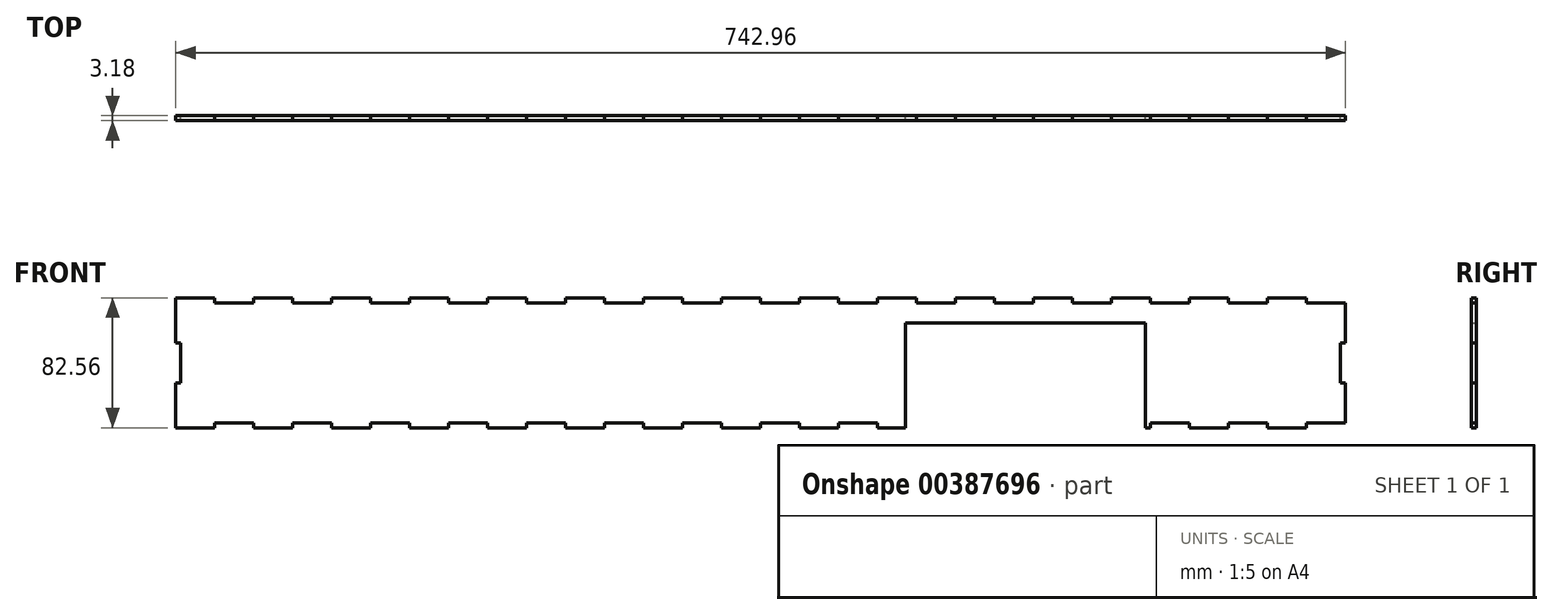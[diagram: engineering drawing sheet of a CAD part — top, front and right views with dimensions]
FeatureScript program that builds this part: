
annotation { "Feature Type Name" : "Feature", "Feature Type Description" : "" }
export const myFeature = defineFeature(function(context is Context, id is Id, definition is map)
    precondition{}
    {
        {
            var Q0;
            Q0=qCreatedBy(makeId("Front.planeOp"),FACE);
            var sketch = newSketch(context, id + "F0", { "sketchPlane" : qUnion([Q0])});
            skLineSegment(sketch, "E0.right", {"start": v(-371.48, -38.1) * mm, "end": v(-371.48, 38.1) * mm, "construction": true});
            skPoint(sketch, "E0.middle", {"position": v(0, 0) * mm});
            skLineSegment(sketch, "E1.top", {"start": v(244.47, 25.4) * mm, "end": v(92.07, 25.4) * mm});
            skLineSegment(sketch, "E1.left", {"start": v(244.47, -38.1) * mm, "end": v(244.47, 25.4) * mm});
            skLineSegment(sketch, "E1.right", {"start": v(92.07, -38.1) * mm, "end": v(92.07, 25.4) * mm});
            skPoint(sketch, "E1.middle", {"position": v(168.28, -6.35) * mm});
            skLineSegment(sketch, "E2.MirrorCS", {"start": v(123.83, 41.28) * mm, "end": v(123.83, 38.1) * mm});
            skLineSegment(sketch, "E3.MirrorCS", {"start": v(-247.65, 41.28) * mm, "end": v(-247.65, 38.1) * mm});
            skLineSegment(sketch, "E4.MirrorCS", {"start": v(272.42, 41.28) * mm, "end": v(272.42, 38.1) * mm});
            skLineSegment(sketch, "E5.MirrorCS", {"start": v(247.65, 41.28) * mm, "end": v(247.65, 38.1) * mm});
            skLineSegment(sketch, "E6.MirrorCS", {"start": v(-297.18, 41.28) * mm, "end": v(-297.18, 38.1) * mm});
            skLineSegment(sketch, "E7.MirrorCS", {"start": v(24.77, 41.28) * mm, "end": v(24.77, 38.1) * mm});
            skLineSegment(sketch, "E8.MirrorCS", {"start": v(-198.12, 41.28) * mm, "end": v(-198.12, 38.1) * mm});
            skLineSegment(sketch, "E9.MirrorCS", {"start": v(-49.53, 41.28) * mm, "end": v(-49.53, 38.1) * mm});
            skLineSegment(sketch, "E10.MirrorCS", {"start": v(222.89, 41.28) * mm, "end": v(222.89, 38.1) * mm});
            skLineSegment(sketch, "E11.MirrorCS", {"start": v(-74.3, 41.28) * mm, "end": v(-74.3, 38.1) * mm});
            skLineSegment(sketch, "E12.MirrorCS", {"start": v(-99.06, 41.28) * mm, "end": v(-99.06, 38.1) * mm});
            skLineSegment(sketch, "E13.MirrorCS", {"start": v(-148.59, 41.28) * mm, "end": v(-148.59, 38.1) * mm});
            skLineSegment(sketch, "E14.MirrorCS", {"start": v(-346.7, 41.28) * mm, "end": v(-346.7, 38.1) * mm});
            skLineSegment(sketch, "E15.MirrorCS", {"start": v(173.36, 41.28) * mm, "end": v(173.36, 38.1) * mm});
            skLineSegment(sketch, "E16.MirrorCS", {"start": v(-321.94, 41.28) * mm, "end": v(-321.94, 38.1) * mm});
            skLineSegment(sketch, "E17.MirrorCS", {"start": v(-123.82, 41.28) * mm, "end": v(-123.82, 38.1) * mm});
            skLineSegment(sketch, "E18.MirrorCS", {"start": v(-272.41, 41.28) * mm, "end": v(-272.41, 38.1) * mm});
            skLineSegment(sketch, "E19.MirrorCS", {"start": v(-173.35, 41.28) * mm, "end": v(-173.35, 38.1) * mm});
            skLineSegment(sketch, "E20.MirrorCS", {"start": v(198.12, 41.28) * mm, "end": v(198.12, 38.1) * mm});
            skLineSegment(sketch, "E21.MirrorCS", {"start": v(-24.76, 41.28) * mm, "end": v(-24.76, 38.1) * mm});
            skLineSegment(sketch, "E22.MirrorCS", {"start": v(74.3, 41.28) * mm, "end": v(74.3, 38.1) * mm});
            skLineSegment(sketch, "E23.MirrorCS", {"start": v(-222.88, 41.28) * mm, "end": v(-222.88, 38.1) * mm});
            skLineSegment(sketch, "E24.MirrorCS", {"start": v(346.71, 41.28) * mm, "end": v(346.71, 38.1) * mm});
            skLineSegment(sketch, "E25.MirrorCS", {"start": v(321.95, 41.28) * mm, "end": v(321.95, 38.1) * mm});
            skLineSegment(sketch, "E26.MirrorCS", {"start": v(297.18, 41.28) * mm, "end": v(297.18, 38.1) * mm});
            skLineSegment(sketch, "E27.MirrorCS", {"start": v(99.06, 41.28) * mm, "end": v(99.06, 38.1) * mm});
            skLineSegment(sketch, "E28.MirrorCS", {"start": v(148.6, 41.28) * mm, "end": v(148.6, 38.1) * mm});
            skLineSegment(sketch, "E29.MirrorCS", {"start": v(49.53, 41.28) * mm, "end": v(49.53, 38.1) * mm});
            skLineSegment(sketch, "E30.MirrorCS", {"start": v(0, 41.28) * mm, "end": v(0, 38.1) * mm});
            skLineSegment(sketch, "E31.MirrorCS", {"start": v(-272.41, 38.1) * mm, "end": v(-297.18, 38.1) * mm});
            skLineSegment(sketch, "E32.MirrorCS", {"start": v(-74.3, 38.1) * mm, "end": v(-99.06, 38.1) * mm});
            skLineSegment(sketch, "E33.MirrorCS", {"start": v(173.36, 38.1) * mm, "end": v(148.6, 38.1) * mm});
            skLineSegment(sketch, "E34.MirrorCS", {"start": v(-148.59, 41.28) * mm, "end": v(-173.35, 41.28) * mm});
            skLineSegment(sketch, "E35.MirrorCS", {"start": v(272.42, 38.1) * mm, "end": v(247.65, 38.1) * mm});
            skLineSegment(sketch, "E36.MirrorCS", {"start": v(24.77, 38.1) * mm, "end": v(0, 38.1) * mm});
            skLineSegment(sketch, "E37.MirrorCS", {"start": v(-198.12, 41.28) * mm, "end": v(-222.88, 41.28) * mm});
            skLineSegment(sketch, "E38.MirrorCS", {"start": v(-173.35, 38.1) * mm, "end": v(-198.12, 38.1) * mm});
            skLineSegment(sketch, "E39.MirrorCS", {"start": v(-24.76, 38.1) * mm, "end": v(-49.53, 38.1) * mm});
            skLineSegment(sketch, "E40.MirrorCS", {"start": v(222.89, 38.1) * mm, "end": v(198.12, 38.1) * mm});
            skLineSegment(sketch, "E41.MirrorCS", {"start": v(74.3, 38.1) * mm, "end": v(49.53, 38.1) * mm});
            skLineSegment(sketch, "E42.MirrorCS", {"start": v(-222.88, 38.1) * mm, "end": v(-247.65, 38.1) * mm});
            skLineSegment(sketch, "E43.MirrorCS", {"start": v(148.6, 41.28) * mm, "end": v(123.83, 41.28) * mm});
            skLineSegment(sketch, "E44.MirrorCS", {"start": v(99.06, 41.28) * mm, "end": v(74.3, 41.28) * mm});
            skLineSegment(sketch, "E45.MirrorCS", {"start": v(0, 41.28) * mm, "end": v(-24.76, 41.28) * mm});
            skLineSegment(sketch, "E46.MirrorCS", {"start": v(-99.06, 41.28) * mm, "end": v(-123.82, 41.28) * mm});
            skLineSegment(sketch, "E47.MirrorCS", {"start": v(123.83, 38.1) * mm, "end": v(99.06, 38.1) * mm});
            skLineSegment(sketch, "E48.MirrorCS", {"start": v(-297.18, 41.28) * mm, "end": v(-321.94, 41.28) * mm});
            skLineSegment(sketch, "E49.MirrorCS", {"start": v(198.12, 41.28) * mm, "end": v(173.36, 41.28) * mm});
            skLineSegment(sketch, "E50.MirrorCS", {"start": v(49.53, 41.28) * mm, "end": v(24.77, 41.28) * mm});
            skLineSegment(sketch, "E51.MirrorCS", {"start": v(-321.94, 38.1) * mm, "end": v(-346.7, 38.1) * mm});
            skLineSegment(sketch, "E52.MirrorCS", {"start": v(-123.82, 38.1) * mm, "end": v(-148.59, 38.1) * mm});
            skLineSegment(sketch, "E53.MirrorCS", {"start": v(346.71, 41.28) * mm, "end": v(321.95, 41.28) * mm});
            skLineSegment(sketch, "E54.MirrorCS", {"start": v(321.95, 38.1) * mm, "end": v(297.18, 38.1) * mm});
            skLineSegment(sketch, "E55.MirrorCS", {"start": v(297.18, 41.28) * mm, "end": v(272.42, 41.28) * mm});
            skLineSegment(sketch, "E56.MirrorCS", {"start": v(-49.53, 41.28) * mm, "end": v(-74.3, 41.28) * mm});
            skLineSegment(sketch, "E57.MirrorCS", {"start": v(-247.65, 41.28) * mm, "end": v(-272.41, 41.28) * mm});
            skLineSegment(sketch, "E58.MirrorCS", {"start": v(247.65, 41.28) * mm, "end": v(222.89, 41.28) * mm});
            skLineSegment(sketch, "E59.MirrorCS", {"start": v(346.71, 38.1) * mm, "end": v(371.48, 38.1) * mm});
            skLineSegment(sketch, "E60.MirrorCS", {"start": v(-346.7, 41.28) * mm, "end": v(-371.47, 41.28) * mm});
            skLineSegment(sketch, "E61", {"start": v(-371.47, 41.28) * mm, "end": v(-371.48, 38.1) * mm});
            skLineSegment(sketch, "E62.top", {"start": v(371.48, -12.7) * mm, "end": v(368.3, -12.7) * mm});
            skLineSegment(sketch, "E62.left", {"start": v(371.48, -38.1) * mm, "end": v(371.48, -12.7) * mm});
            skLineSegment(sketch, "E63.bottom", {"start": v(368.3, -12.7) * mm, "end": v(371.48, -12.7) * mm});
            skLineSegment(sketch, "E63.top", {"start": v(368.3, 12.7) * mm, "end": v(371.48, 12.7) * mm});
            skLineSegment(sketch, "E63.left", {"start": v(368.3, -12.7) * mm, "end": v(368.3, 12.7) * mm});
            skLineSegment(sketch, "E64.bottom", {"start": v(371.48, 12.7) * mm, "end": v(368.3, 12.7) * mm});
            skLineSegment(sketch, "E64.top", {"start": v(371.48, 38.1) * mm, "end": v(368.3, 38.1) * mm});
            skLineSegment(sketch, "E64.left", {"start": v(371.48, 12.7) * mm, "end": v(371.48, 38.1) * mm});
            skLineSegment(sketch, "E65.MirrorCS", {"start": v(-371.48, -38.1) * mm, "end": v(-371.48, -12.7) * mm});
            skLineSegment(sketch, "E66.MirrorCS", {"start": v(-368.3, -12.7) * mm, "end": v(-371.48, -12.7) * mm});
            skLineSegment(sketch, "E67.MirrorCS", {"start": v(-368.3, -12.7) * mm, "end": v(-368.3, 12.7) * mm});
            skLineSegment(sketch, "E68.MirrorCS", {"start": v(-368.3, 12.7) * mm, "end": v(-371.48, 12.7) * mm});
            skLineSegment(sketch, "E69", {"start": v(-371.48, 12.7) * mm, "end": v(-371.48, 38.1) * mm});
            skLineSegment(sketch, "E70.MirrorCS", {"start": v(272.41, -41.28) * mm, "end": v(272.41, -38.1) * mm});
            skLineSegment(sketch, "E71.MirrorCS", {"start": v(-74.3, -41.28) * mm, "end": v(-74.3, -38.1) * mm});
            skLineSegment(sketch, "E72.MirrorCS", {"start": v(346.7, -41.28) * mm, "end": v(321.94, -41.28) * mm});
            skLineSegment(sketch, "E73.MirrorCS", {"start": v(-198.12, -41.28) * mm, "end": v(-222.89, -41.28) * mm});
            skLineSegment(sketch, "E74.MirrorCS", {"start": v(-24.77, -41.28) * mm, "end": v(-24.77, -38.1) * mm});
            skLineSegment(sketch, "E75.MirrorCS", {"start": v(-198.12, -41.28) * mm, "end": v(-198.12, -38.1) * mm});
            skLineSegment(sketch, "E76.MirrorCS", {"start": v(0, -41.28) * mm, "end": v(0, -38.1) * mm});
            skLineSegment(sketch, "E77.MirrorCS", {"start": v(-99.06, -41.28) * mm, "end": v(-123.83, -41.28) * mm});
            skLineSegment(sketch, "E78.MirrorCS", {"start": v(-346.71, -41.28) * mm, "end": v(-346.71, -38.1) * mm});
            skLineSegment(sketch, "E79.MirrorCS", {"start": v(24.76, -41.28) * mm, "end": v(24.76, -38.1) * mm});
            skLineSegment(sketch, "E80.MirrorCS", {"start": v(247.65, -41.28) * mm, "end": v(247.65, -38.1) * mm});
            skLineSegment(sketch, "E81.MirrorCS", {"start": v(-49.53, -41.28) * mm, "end": v(-74.3, -41.28) * mm});
            skLineSegment(sketch, "E82.MirrorCS", {"start": v(-222.89, -41.28) * mm, "end": v(-222.89, -38.1) * mm});
            skLineSegment(sketch, "E83.MirrorCS", {"start": v(-321.95, -41.28) * mm, "end": v(-321.95, -38.1) * mm});
            skLineSegment(sketch, "E84.MirrorCS", {"start": v(-123.83, -41.28) * mm, "end": v(-123.83, -38.1) * mm});
            skLineSegment(sketch, "E85.MirrorCS", {"start": v(-99.06, -41.28) * mm, "end": v(-99.06, -38.1) * mm});
            skLineSegment(sketch, "E86.MirrorCS", {"start": v(0, -41.28) * mm, "end": v(-24.77, -41.28) * mm});
            skLineSegment(sketch, "E87.MirrorCS", {"start": v(49.53, -41.28) * mm, "end": v(49.53, -38.1) * mm});
            skLineSegment(sketch, "E88.MirrorCS", {"start": v(-173.36, -41.28) * mm, "end": v(-173.36, -38.1) * mm});
            skLineSegment(sketch, "E89.MirrorCS", {"start": v(-297.18, -41.28) * mm, "end": v(-297.18, -38.1) * mm});
            skLineSegment(sketch, "E90.MirrorCS", {"start": v(-247.65, -41.28) * mm, "end": v(-272.42, -41.28) * mm});
            skLineSegment(sketch, "E91.MirrorCS", {"start": v(346.7, -41.28) * mm, "end": v(346.7, -38.1) * mm});
            skLineSegment(sketch, "E92.MirrorCS", {"start": v(-148.6, -41.28) * mm, "end": v(-148.6, -38.1) * mm});
            skLineSegment(sketch, "E93.MirrorCS", {"start": v(-247.65, -41.28) * mm, "end": v(-247.65, -38.1) * mm});
            skLineSegment(sketch, "E94.MirrorCS", {"start": v(49.53, -41.28) * mm, "end": v(24.76, -41.28) * mm});
            skLineSegment(sketch, "E95.MirrorCS", {"start": v(74.3, -41.28) * mm, "end": v(74.3, -38.1) * mm});
            skLineSegment(sketch, "E96.MirrorCS", {"start": v(-272.42, -41.28) * mm, "end": v(-272.42, -38.1) * mm});
            skLineSegment(sketch, "E97.MirrorCS", {"start": v(-148.6, -41.28) * mm, "end": v(-173.36, -41.28) * mm});
            skLineSegment(sketch, "E98.MirrorCS", {"start": v(-297.18, -41.28) * mm, "end": v(-321.95, -41.28) * mm});
            skLineSegment(sketch, "E99.MirrorCS", {"start": v(-49.53, -41.28) * mm, "end": v(-49.53, -38.1) * mm});
            skLineSegment(sketch, "E100.MirrorCS", {"start": v(297.18, -41.28) * mm, "end": v(297.18, -38.1) * mm});
            skLineSegment(sketch, "E101.MirrorCS", {"start": v(297.18, -41.28) * mm, "end": v(272.41, -41.28) * mm});
            skLineSegment(sketch, "E102.MirrorCS", {"start": v(321.94, -41.28) * mm, "end": v(321.94, -38.1) * mm});
            skLineSegment(sketch, "E103.MirrorCS", {"start": v(-346.71, -41.28) * mm, "end": v(-371.48, -41.28) * mm});
            skLineSegment(sketch, "E104.MirrorCS", {"start": v(24.76, -38.1) * mm, "end": v(0, -38.1) * mm});
            skLineSegment(sketch, "E105.MirrorCS", {"start": v(-123.83, -38.1) * mm, "end": v(-148.6, -38.1) * mm});
            skLineSegment(sketch, "E106.MirrorCS", {"start": v(346.7, -38.1) * mm, "end": v(371.47, -38.1) * mm});
            skLineSegment(sketch, "E107.MirrorCS", {"start": v(-272.42, -38.1) * mm, "end": v(-297.18, -38.1) * mm});
            skLineSegment(sketch, "E108.MirrorCS", {"start": v(-173.36, -38.1) * mm, "end": v(-198.12, -38.1) * mm});
            skLineSegment(sketch, "E109.MirrorCS", {"start": v(272.41, -38.1) * mm, "end": v(247.65, -38.1) * mm});
            skLineSegment(sketch, "E110.MirrorCS", {"start": v(-321.95, -38.1) * mm, "end": v(-346.71, -38.1) * mm});
            skLineSegment(sketch, "E111.MirrorCS", {"start": v(74.3, -38.1) * mm, "end": v(49.53, -38.1) * mm});
            skLineSegment(sketch, "E112.MirrorCS", {"start": v(321.94, -38.1) * mm, "end": v(297.18, -38.1) * mm});
            skLineSegment(sketch, "E113.MirrorCS", {"start": v(-222.89, -38.1) * mm, "end": v(-247.65, -38.1) * mm});
            skLineSegment(sketch, "E114.MirrorCS", {"start": v(-24.77, -38.1) * mm, "end": v(-49.53, -38.1) * mm});
            skLineSegment(sketch, "E115.MirrorCS", {"start": v(-74.3, -38.1) * mm, "end": v(-99.06, -38.1) * mm});
            skLineSegment(sketch, "E116", {"start": v(-371.48, -38.1) * mm, "end": v(-371.48, -41.28) * mm});
            skLineSegment(sketch, "E117", {"start": v(244.47, -38.1) * mm, "end": v(244.47, -41.28) * mm});
            skLineSegment(sketch, "E118", {"start": v(92.07, -38.1) * mm, "end": v(92.07, -41.28) * mm});
            skLineSegment(sketch, "E119", {"start": v(244.47, -41.28) * mm, "end": v(247.65, -41.28) * mm});
            skLineSegment(sketch, "E120", {"start": v(92.07, -41.28) * mm, "end": v(74.3, -41.28) * mm});
            skSolve(sketch);
        }
        {
            var Q0;
            Q0=qSketchRegion(id+"F0",true);
            extrude(context, id + "F1", {"entities" : qUnion([Q0]), "depth" : 3.17 * mm});
        }
    });
